# Revit family: Gira_028603
name_source: partatom
category: Electrical Fixtures
revit_build: Autodesk Revit 2017 (Build: 20160225_1515(x64)
units: mm (PartAtom-declared; Revit-internal decimal feet)

## family parameters
Cut with Voids When Loaded = No
Host = Face
Maintain Annotation Orientation = No
Part Type = Normal
Room Calculation Point = No
Round Connector Dimension = Use Diameter
Shared = No

## types (1)
- Wippe Symb. Klingel System 55 Reinweiß
    Abtastbares Symbol/barrierefrei = No
    Aufdruck/Kennzeichnung = Symbol "Klingel"
    Ausführung = einteilige Wippe
    Ausführung der Oberfläche = glänzend
    Available = Yes
    Befestigungsart = Klemmbefestigung
    Category = Abdeckung/Bedienelement für Installationsschalterprogramme
    Data sheet (1) = https://katalog.gira.de
    Default Elevation = 1219 mm
    Farbe = weiß
    GTIN = 4010337286035
    Geeignet für Bussystem-Tasterankopplung = No
    Geeignet für Schutzart (IP) = IP20
    HAN = 028603
    Halogenfrei = Yes
    HeinzeBIM = https://bimportal.heinze.de
    Keynote = Sys55_Abdeckung_Schalten und Tasten
    Kontrollfenster/Lichtauslass = No
    Manufacturer URL = https://www.gira.de
    Mit Beschriftungsfeld = No
    Mit austauschbarer Linse/Symbol = No
    Name = Wippe Symb. Klingel System 55 Reinweiß
    Oberfläche = sonstige
    RAL-Nummer (ähnlich) = 9010
    Region = DE
    URL = http://katalog.gira.de
    Verwendung = Schalter/Taster
    Werkstoff = Kunststoff
    Werkstoffgüte = Thermoplast

## geometry (parser evidence)
native form markers: Blend x2, Sweep x7
no freeform markers — native parametric forms only
